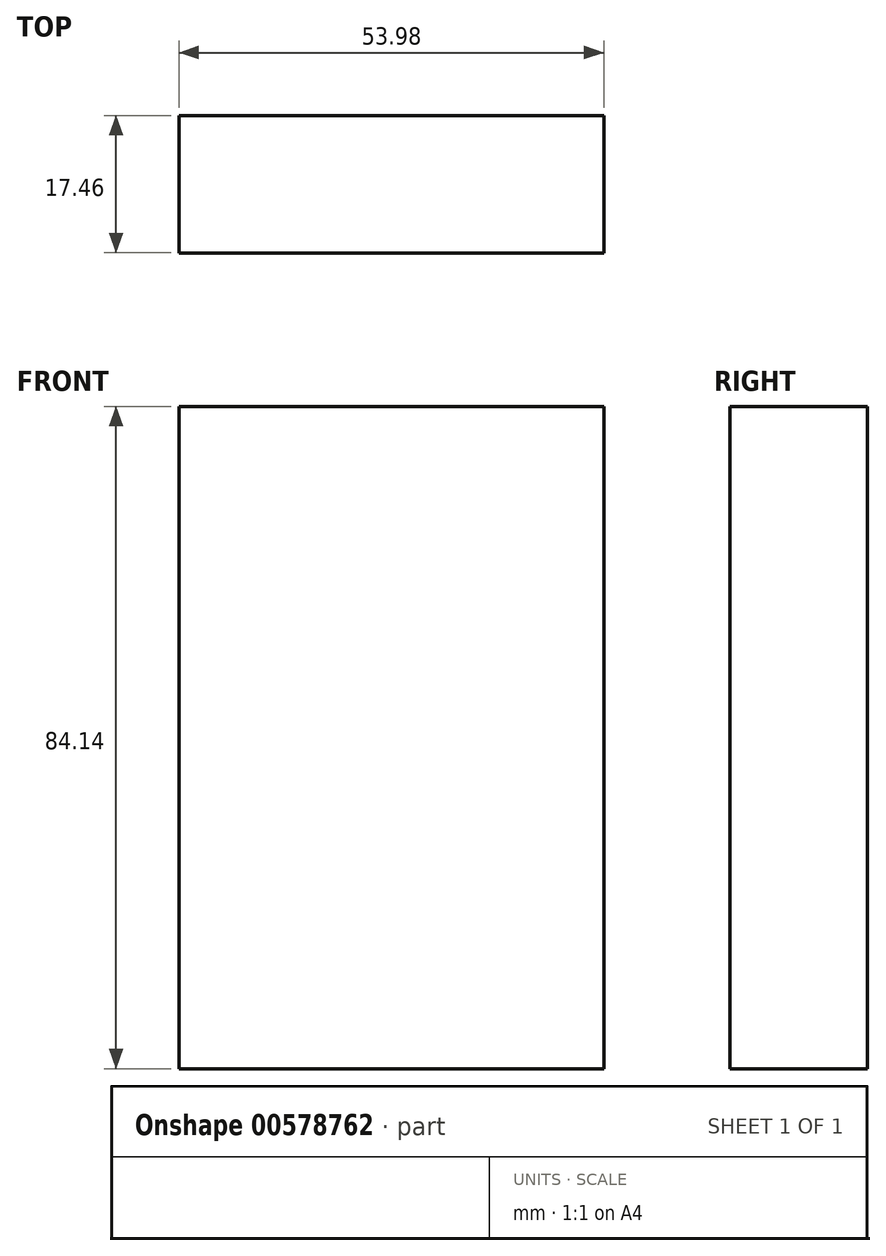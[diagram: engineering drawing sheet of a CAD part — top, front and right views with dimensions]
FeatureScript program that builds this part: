
annotation { "Feature Type Name" : "Feature", "Feature Type Description" : "" }
export const myFeature = defineFeature(function(context is Context, id is Id, definition is map)
    precondition{}
    {
        {
            var Q0;
            Q0=qCreatedBy(makeId("Front.planeOp"),FACE);
            var sketch = newSketch(context, id + "F0", { "sketchPlane" : qUnion([Q0])});
            skLineSegment(sketch, "E0.bottom", {"start": v(0, 0) * mm, "end": v(53.98, 0) * mm});
            skLineSegment(sketch, "E0.top", {"start": v(0, 84.14) * mm, "end": v(53.97, 84.14) * mm});
            skLineSegment(sketch, "E0.left", {"start": v(0, 0) * mm, "end": v(0, 84.14) * mm});
            skLineSegment(sketch, "E0.right", {"start": v(53.98, 0) * mm, "end": v(53.97, 84.14) * mm});
            skSolve(sketch);
        }
        {
            var Q0;
            Q0 = qSketchRegion(id + "F0", true);
            extrude(context, id + "F1", {"entities" : qUnion([Q0]), "depth" : 17.46 * mm, "offsetDistance" : 25.4 * mm});
        }
    });
